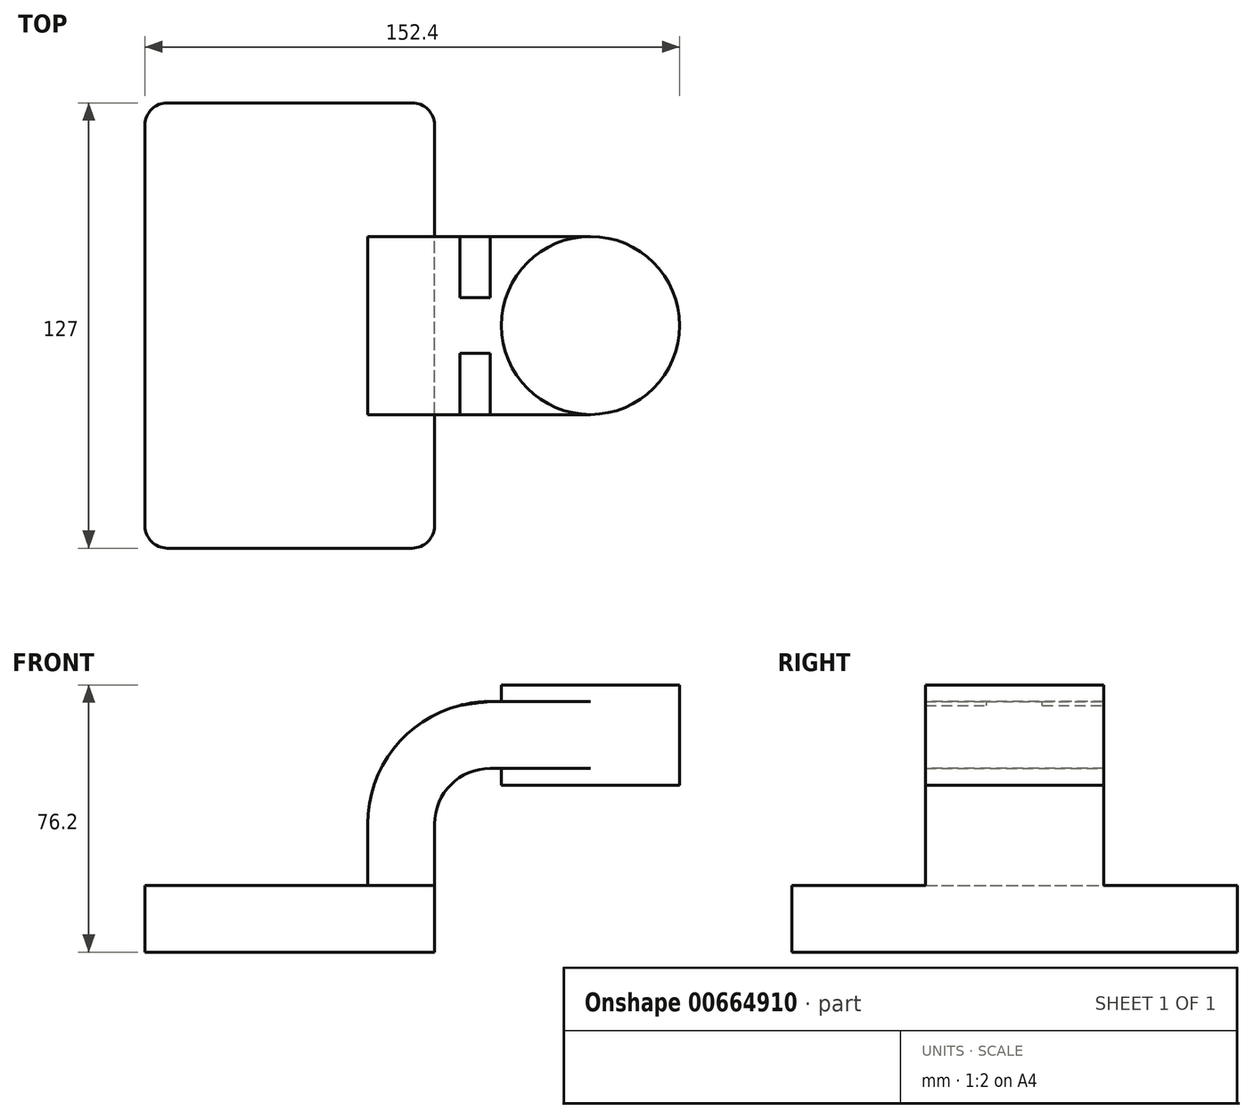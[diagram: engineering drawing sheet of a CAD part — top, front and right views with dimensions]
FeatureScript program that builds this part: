
annotation { "Feature Type Name" : "Feature", "Feature Type Description" : "" }
export const myFeature = defineFeature(function(context is Context, id is Id, definition is map)
    precondition{}
    {
        {
            var Q0;
            Q0=qCreatedBy(makeId("Front.planeOp"),FACE);
            var sketch = newSketch(context, id + "F0", { "sketchPlane" : qUnion([Q0])});
            skLineSegment(sketch, "E0.bottom", {"start": v(-41.28, 19.05) * mm, "end": v(41.28, 19.05) * mm});
            skLineSegment(sketch, "E0.top", {"start": v(-41.28, 0) * mm, "end": v(41.28, 0) * mm});
            skLineSegment(sketch, "E0.left", {"start": v(-41.28, 19.05) * mm, "end": v(-41.28, 0) * mm});
            skLineSegment(sketch, "E0.right", {"start": v(41.28, 19.05) * mm, "end": v(41.28, 0) * mm});
            skLineSegment(sketch, "E1.bottom", {"start": v(60.33, 76.2) * mm, "end": v(111.12, 76.2) * mm});
            skLineSegment(sketch, "E1.top", {"start": v(60.33, 47.62) * mm, "end": v(111.12, 47.62) * mm});
            skLineSegment(sketch, "E1.left", {"start": v(60.33, 76.2) * mm, "end": v(60.32, 47.62) * mm});
            skLineSegment(sketch, "E1.right", {"start": v(111.13, 76.2) * mm, "end": v(111.12, 47.62) * mm});
            skLineSegment(sketch, "E2", {"start": v(41.28, 19.05) * mm, "end": v(41.28, 36.53) * mm});
            skArc(sketch, "E3", {"start": v(41.28, 36.53) * mm, "mid": v(45.92, 47.75) * mm, "end": v(57.15, 52.4) * mm});
            skLineSegment(sketch, "E4", {"start": v(57.15, 52.4) * mm, "end": v(85.73, 52.4) * mm});
            skPoint(sketch, "E5", {"position": v(85.73, 61.91) * mm});
            skPoint(sketch, "E5.positionSnap0", {"position": v(60.33, 61.91) * mm});
            skPoint(sketch, "E5.positionSnap1", {"position": v(85.73, 76.2) * mm});
            skLineSegment(sketch, "E6.0", {"start": v(57.15, 71.45) * mm, "end": v(85.73, 71.45) * mm});
            skArc(sketch, "E6.1", {"start": v(22.23, 36.53) * mm, "mid": v(32.45, 61.22) * mm, "end": v(57.15, 71.45) * mm});
            skLineSegment(sketch, "E6.2", {"start": v(22.23, 19.05) * mm, "end": v(22.23, 36.53) * mm});
            skFitSpline(sketch, "E7", {"points": [v(-41.28, 19.05) * mm, v(57.15, 71.45) * mm], "startDerivative": vector(0.6, 90.77) * mm, "endDerivative": vector(81, 6.7) * mm});
            skLineSegment(sketch, "E8", {"start": v(85.73, 76.2) * mm, "end": v(85.73, 47.62) * mm});
            skSolve(sketch);
        }
        {
            var Q0;
            Q0=makeQuery(id+"F0.imprint","IMPRINT",FACE,{"disambiguationData":[TD([[makeQuery(id+"F0.imprint","IMPRINT",EDGE,{"derivedFrom":sQuery(id+"F0.wireOp",EDGE,"E0.top")}),1.0]])]});
            extrude(context, id + "F1", {"entities" : qUnion([Q0]), "endBound" : BoundingType.SYMMETRIC, "depth" : 127 * mm, "offsetDistance" : 25.4 * mm});
        }
        {
            var Q0;
            {var subQ1=sQuery(id+"F0.wireOp",EDGE,"E2");Q0=makeQuery(id+"F0.imprint","IMPRINT",FACE,{"disambiguationData":[TD([[makeQuery(id+"F0.imprint","IMPRINT",EDGE,{"derivedFrom":subQ1}),1.0]])]});}
            var Q1;
            {var subQ0=sQuery(id+"F0.wireOp",EDGE,"E6.0");var subQ1=sQuery(id+"F0.wireOp",EDGE,"E1.left");var subQ2=makeQuery(id+"F0.imprint","INTERSECT",VERTEX,{"derivedFrom":[subQ1,subQ0]});Q1=makeQuery(id+"F0.imprint","IMPRINT",FACE,{"disambiguationData":[TD([[makeQuery(id+"F0.imprint","IMPRINT",EDGE,{"disambiguationData":[TD([[subQ2,-1.0]])],"derivedFrom":subQ1}),1.0]])]});}
            extrude(context, id + "F2", {"entities" : qUnion([Q0, Q1]), "operationType" : NewBodyOperationType.ADD, "endBound" : BoundingType.SYMMETRIC, "depth" : 50.8 * mm, "offsetDistance" : 25.4 * mm});
        }
        {
            var Q0;
            Q0=makeQuery(id+"F0.imprint","IMPRINT",FACE,{"disambiguationData":[TD([[makeQuery(id+"F0.imprint","IMPRINT",EDGE,{"derivedFrom":sQuery(id+"F0.wireOp",EDGE,"E6.1")}),1.0]])]});
            extrude(context, id + "F3", {"entities" : qUnion([Q0]), "operationType" : NewBodyOperationType.ADD, "endBound" : BoundingType.SYMMETRIC, "depth" : 15.88 * mm, "offsetDistance" : 25.4 * mm});
        }
        {
            var Q0;
            Q0=makeQuery(id+"F1.opExtrude","CAP_EDGE",EDGE,{"disambiguationData":[OSD([sQuery(id+"F0.wireOp",EDGE,"E0.right")])],"isStart":false});
            var Q1;
            Q1=makeQuery(id+"F1.opExtrude","CAP_EDGE",EDGE,{"disambiguationData":[OSD([sQuery(id+"F0.wireOp",EDGE,"E0.left")])],"isStart":false});
            var Q2;
            Q2=makeQuery(id+"F1.opExtrude","CAP_EDGE",EDGE,{"disambiguationData":[OSD([sQuery(id+"F0.wireOp",EDGE,"E0.left")])],"isStart":true});
            var Q3;
            Q3=makeQuery(id+"F1.opExtrude","CAP_EDGE",EDGE,{"disambiguationData":[OSD([sQuery(id+"F0.wireOp",EDGE,"E0.right")])],"isStart":true});
            fillet(context, id + "F4", {"entities" : qUnion([Q0, Q1, Q2, Q3]), "radius" : 6.35 * mm, "tangentPropagation" : true, "allowEdgeOverflow" : false});
        }
        {
            var Q0;
            {var subQ4=sQuery(id+"F0.wireOp",EDGE,"E1.right");Q0=makeQuery(id+"F0.imprint","IMPRINT",FACE,{"disambiguationData":[TD([[makeQuery(id+"F0.imprint","IMPRINT",EDGE,{"derivedFrom":subQ4}),-1.0]])]});}
            var Q1;
            Q1=sQuery(id+"F0.wireOp",EDGE,"E8");
            revolve(context, id + "F5", {"operationType" : NewBodyOperationType.ADD, "entities" : qUnion([Q0]), "axis" : qUnion([Q1]), "revolveType" : RevolveType.FULL});
        }
    });
